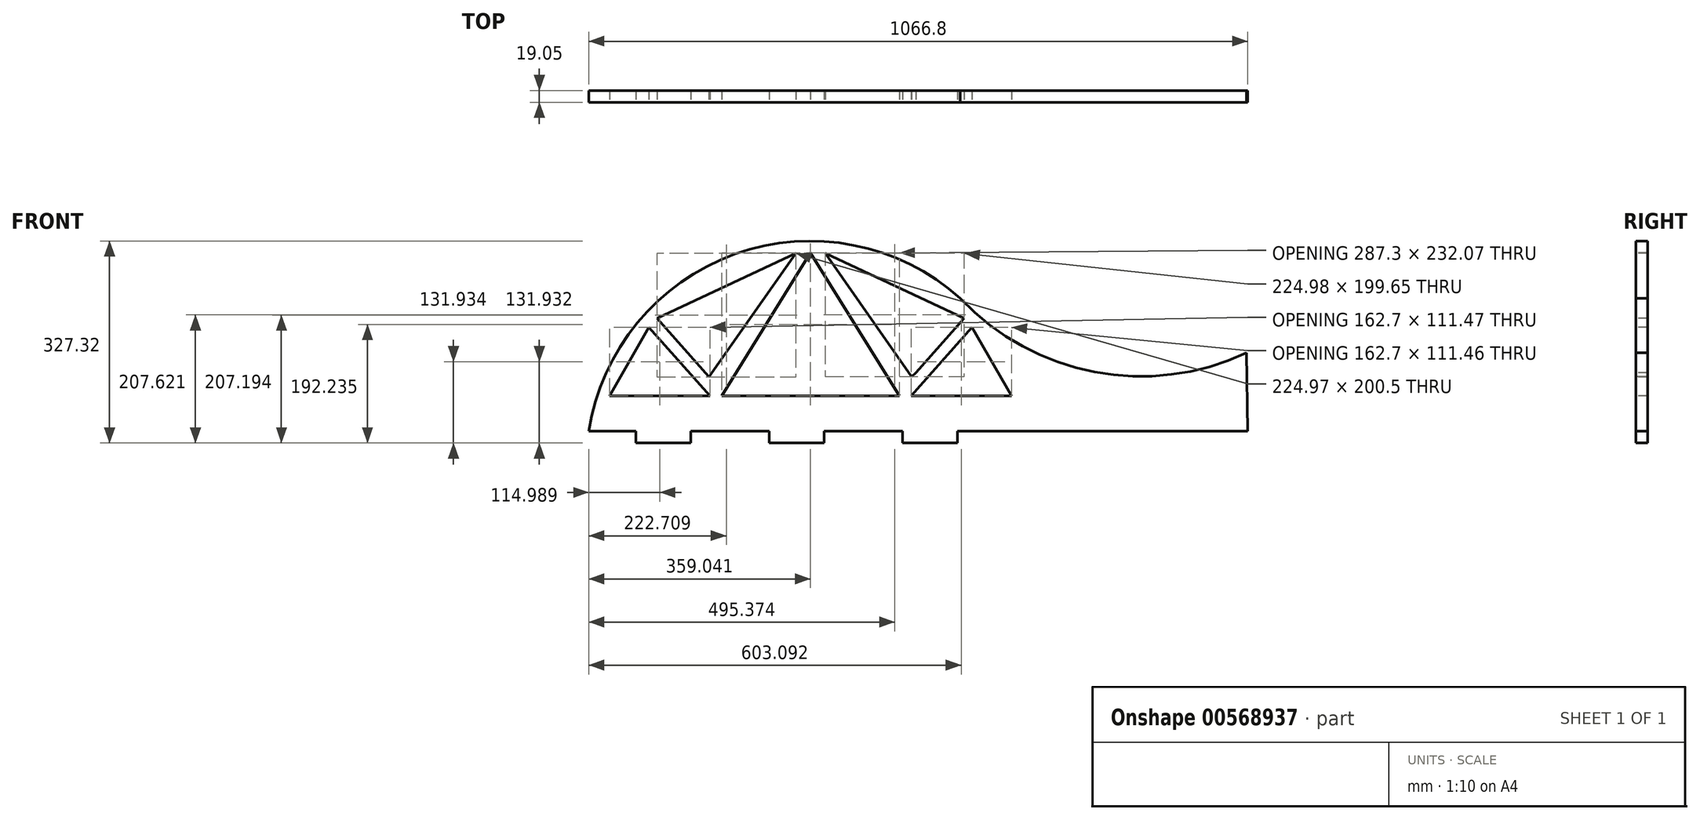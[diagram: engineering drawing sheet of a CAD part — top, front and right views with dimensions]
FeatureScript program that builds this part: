
annotation { "Feature Type Name" : "Feature", "Feature Type Description" : "" }
export const myFeature = defineFeature(function(context is Context, id is Id, definition is map)
    precondition{}
    {
        {
            var Q0;
            Q0=qCreatedBy(makeId("Front.planeOp"),FACE);
            var sketch = newSketch(context, id + "F0", { "sketchPlane" : qUnion([Q0])});
            skLineSegment(sketch, "E0", {"start": v(1219.75, -127) * mm, "end": v(152.95, -127) * mm});
            skPoint(sketch, "E1", {"position": v(512, -181.95) * mm});
            skArc(sketch, "E2", {"start": v(152.95, -127) * mm, "mid": v(389.49, 159.99) * mm, "end": v(754.45, 88.5) * mm});
            skArc(sketch, "E3", {"start": v(754.45, 88.5) * mm, "mid": v(971.96, -30.97) * mm, "end": v(1218.13, 0.3) * mm});
            skLineSegment(sketch, "E4", {"start": v(1218.13, 0.3) * mm, "end": v(1219.75, -127) * mm});
            skLineSegment(sketch, "E5", {"start": v(754.45, 88.5) * mm, "end": v(754.45, -127) * mm});
            skLineSegment(sketch, "E6", {"start": v(754.45, -127) * mm, "end": v(1219.75, -127) * mm});
            skSolve(sketch);
        }
        {
            var Q0;
            Q0=qSketchRegion(id+"F0",true);
            extrude(context, id + "F1", {"entities" : qUnion([Q0]), "depth" : 19.05 * mm, "offsetDistance" : 25.4 * mm});
        }
        {
            var Q0;
            Q0=makeQuery(id+"F1.opExtrude","CAP_FACE",FACE,{"disambiguationData":[OSD([sQuery(id+"F0.wireOp",EDGE,"E0"),sQuery(id+"F0.wireOp",EDGE,"E2"),sQuery(id+"F0.wireOp",EDGE,"E3"),sQuery(id+"F0.wireOp",EDGE,"E4"),sQuery(id+"F0.wireOp",EDGE,"E6")])],"isStart":false});
            var sketch = newSketch(context, id + "F2", { "sketchPlane" : qUnion([Q0])});
            skLineSegment(sketch, "E7", {"start": v(250.32, 41.62) * mm, "end": v(186.59, -69.85) * mm});
            skLineSegment(sketch, "E8", {"start": v(773.66, 41.61) * mm, "end": v(837.4, -69.85) * mm});
            skLineSegment(sketch, "E9", {"start": v(313.4, -69.85) * mm, "end": v(314.05, -69.85) * mm});
            skLineSegment(sketch, "E10", {"start": v(250.32, -127) * mm, "end": v(250.32, -69.85) * mm});
            skPoint(sketch, "E10.startSnap0", {"position": v(250.32, -69.85) * mm});
            skCircle(sketch, "E11", {"center": v(250.32, -98.43) * mm, "radius": 9.78 * mm});
            skLineSegment(sketch, "E12", {"start": v(250.32, 41.62) * mm, "end": v(349.29, -69.85) * mm});
            skLineSegment(sketch, "E13", {"start": v(773.66, 41.61) * mm, "end": v(674.7, -69.85) * mm});
            skLineSegment(sketch, "E14", {"start": v(456.77, 116.65) * mm, "end": v(398.77, 33.92) * mm});
            skLineSegment(sketch, "E15", {"start": v(275.35, 42.12) * mm, "end": v(321.76, -10.16) * mm});
            skLineSegment(sketch, "E16", {"start": v(398.77, 33.92) * mm, "end": v(349.29, -36.67) * mm});
            skLineSegment(sketch, "E17", {"start": v(321.76, -10.16) * mm, "end": v(345.3, -36.67) * mm});
            skLineSegment(sketch, "E18", {"start": v(345.3, -36.67) * mm, "end": v(347.07, -38.66) * mm});
            skLineSegment(sketch, "E19", {"start": v(349.29, -36.67) * mm, "end": v(347.58, -39.1) * mm});
            skLineSegment(sketch, "E20", {"start": v(347.58, -39.1) * mm, "end": v(347.07, -38.66) * mm});
            skLineSegment(sketch, "E21", {"start": v(275.35, 42.12) * mm, "end": v(263.17, 55.84) * mm});
            skLineSegment(sketch, "E22", {"start": v(456.77, 116.65) * mm, "end": v(488.15, 161.4) * mm});
            skLineSegment(sketch, "E23", {"start": v(488.15, 161.4) * mm, "end": v(263.17, 55.84) * mm});
            skLineSegment(sketch, "E24", {"start": v(558.16, 129.54) * mm, "end": v(618.05, 44.13) * mm});
            skLineSegment(sketch, "E25", {"start": v(738.86, 31.1) * mm, "end": v(696.51, -16.58) * mm});
            skLineSegment(sketch, "E26", {"start": v(696.51, -16.58) * mm, "end": v(738.86, 31.1) * mm});
            skLineSegment(sketch, "E27", {"start": v(558.16, 129.54) * mm, "end": v(535.84, 161.4) * mm});
            skLineSegment(sketch, "E28", {"start": v(738.86, 31.1) * mm, "end": v(760.81, 55.83) * mm});
            skLineSegment(sketch, "E29", {"start": v(760.81, 55.83) * mm, "end": v(535.84, 161.4) * mm});
            skLineSegment(sketch, "E30", {"start": v(696.51, -16.58) * mm, "end": v(682.48, -32.39) * mm});
            skLineSegment(sketch, "E31", {"start": v(618.05, 44.13) * mm, "end": v(675.8, -38.25) * mm});
            skLineSegment(sketch, "E32", {"start": v(675.8, -38.25) * mm, "end": v(682.48, -32.39) * mm});
            skLineSegment(sketch, "E33", {"start": v(186.59, -69.85) * mm, "end": v(349.29, -69.85) * mm});
            skLineSegment(sketch, "E34", {"start": v(368.34, -69.85) * mm, "end": v(655.64, -69.85) * mm});
            skLineSegment(sketch, "E35", {"start": v(674.7, -69.85) * mm, "end": v(837.4, -69.85) * mm});
            skLineSegment(sketch, "E36", {"start": v(512, 162.22) * mm, "end": v(368.34, -69.85) * mm});
            skLineSegment(sketch, "E37", {"start": v(512, 162.22) * mm, "end": v(655.64, -69.85) * mm});
            skSolve(sketch);
        }
        {
            var Q0;
            {var subQ3=sQuery(id+"F2.wireOp",EDGE,"E7");Q0=makeQuery(id+"F2.imprint","IMPRINT",FACE,{"disambiguationData":[TD([[makeQuery(id+"F2.imprint","IMPRINT",EDGE,{"derivedFrom":subQ3}),1.0]])]});}
            var Q1;
            Q1=makeQuery(id+"F2.imprint","IMPRINT",FACE,{"disambiguationData":[TD([[makeQuery(id+"F2.imprint","IMPRINT",EDGE,{"derivedFrom":sQuery(id+"F2.wireOp",EDGE,"E14")}),-1.0]])]});
            var Q2;
            Q2=makeQuery(id+"F2.imprint","IMPRINT",FACE,{"disambiguationData":[TD([[makeQuery(id+"F2.imprint","IMPRINT",EDGE,{"derivedFrom":sQuery(id+"F2.wireOp",EDGE,"E34")}),1.0]])]});
            var Q3;
            Q3=makeQuery(id+"F2.imprint","IMPRINT",FACE,{"disambiguationData":[TD([[makeQuery(id+"F2.imprint","IMPRINT",EDGE,{"derivedFrom":sQuery(id+"F2.wireOp",EDGE,"E24")}),1.0]])]});
            var Q4;
            Q4=makeQuery(id+"F2.imprint","IMPRINT",FACE,{"disambiguationData":[TD([[makeQuery(id+"F2.imprint","IMPRINT",EDGE,{"derivedFrom":sQuery(id+"F2.wireOp",EDGE,"E8")}),-1.0]])]});
            extrude(context, id + "F3", {"entities" : qUnion([Q0, Q1, Q2, Q3, Q4]), "operationType" : NewBodyOperationType.REMOVE, "oppositeDirection" : true, "depth" : 25.4 * mm, "offsetDistance" : 25.4 * mm});
        }
        {
            var Q0;
            {var subQ4=sQuery(id+"F2.wireOp",EDGE,"E7");Q0=makeQuery(id+"F2.imprint","IMPRINT",FACE,{"disambiguationData":[TD([[makeQuery(id+"F2.imprint","IMPRINT",EDGE,{"derivedFrom":subQ4}),-1.0]])]});}
            var sketch = newSketch(context, id + "F4", { "sketchPlane" : qUnion([Q0])});
            skLineSegment(sketch, "E38.0", {"start": v(1219.75, -127) * mm, "end": v(152.95, -127) * mm});
            skLineSegment(sketch, "E39.bottom", {"start": v(660.95, -127) * mm, "end": v(749.85, -127) * mm});
            skLineSegment(sketch, "E39.top", {"start": v(660.95, -146.05) * mm, "end": v(749.85, -146.05) * mm});
            skLineSegment(sketch, "E39.left", {"start": v(660.95, -127) * mm, "end": v(660.95, -146.05) * mm});
            skLineSegment(sketch, "E39.right", {"start": v(749.85, -127) * mm, "end": v(749.85, -146.05) * mm});
            skLineSegment(sketch, "E40.bottom", {"start": v(445.05, -127) * mm, "end": v(533.95, -127) * mm});
            skLineSegment(sketch, "E40.top", {"start": v(445.05, -146.05) * mm, "end": v(533.95, -146.05) * mm});
            skLineSegment(sketch, "E40.left", {"start": v(445.05, -127) * mm, "end": v(445.05, -146.05) * mm});
            skLineSegment(sketch, "E40.right", {"start": v(533.95, -127) * mm, "end": v(533.95, -146.05) * mm});
            skLineSegment(sketch, "E41.bottom", {"start": v(229.15, -127) * mm, "end": v(318.05, -127) * mm});
            skLineSegment(sketch, "E41.top", {"start": v(229.15, -146.05) * mm, "end": v(318.05, -146.05) * mm});
            skLineSegment(sketch, "E41.left", {"start": v(229.15, -127) * mm, "end": v(229.15, -146.05) * mm});
            skLineSegment(sketch, "E41.right", {"start": v(318.05, -127) * mm, "end": v(318.05, -146.05) * mm});
            skSolve(sketch);
        }
        {
            var Q0;
            Q0 = qSketchRegion(id + "F4", true);
            extrude(context, id + "F5", {"entities" : qUnion([Q0]), "operationType" : NewBodyOperationType.ADD, "oppositeDirection" : true, "depth" : 19.05 * mm, "offsetDistance" : 25.4 * mm});
        }
    });
